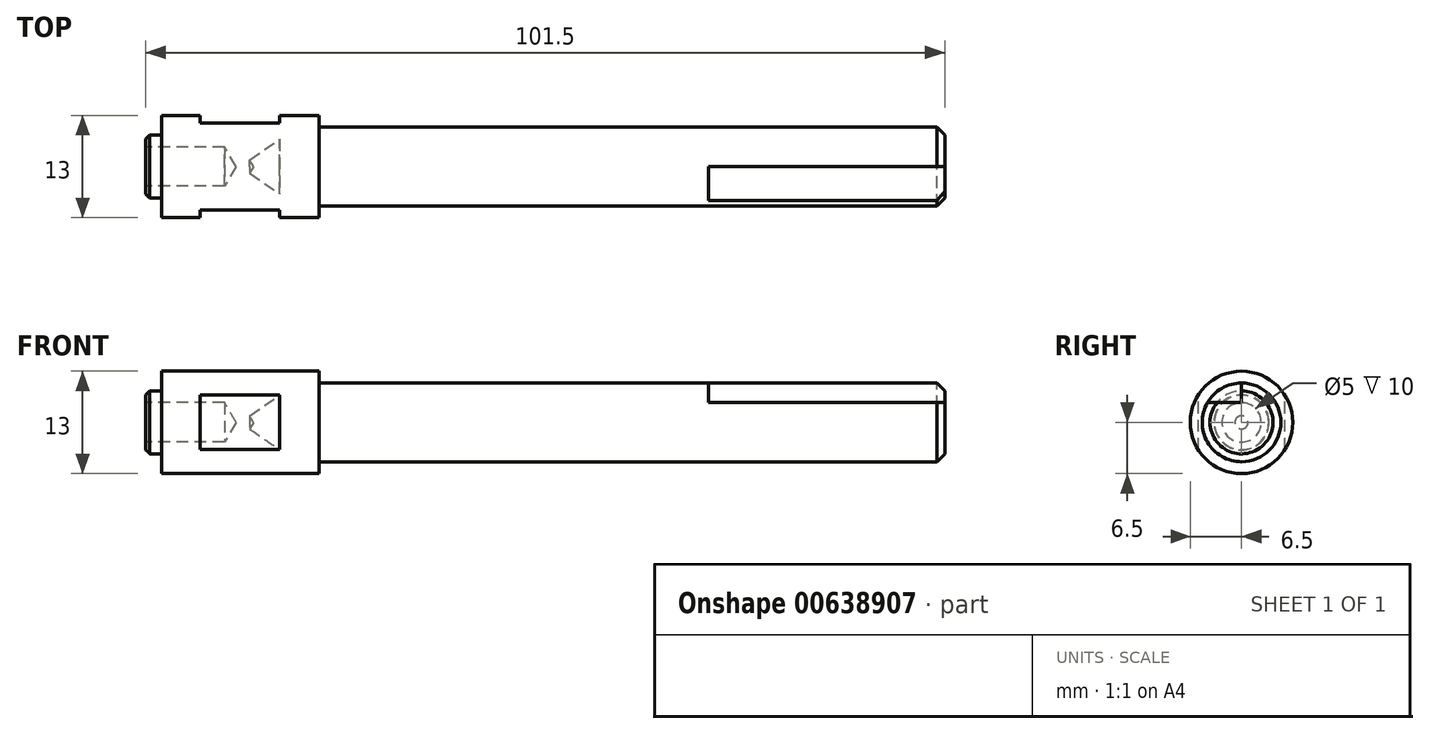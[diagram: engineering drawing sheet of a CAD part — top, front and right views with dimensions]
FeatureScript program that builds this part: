
annotation { "Feature Type Name" : "Feature", "Feature Type Description" : "" }
export const myFeature = defineFeature(function(context is Context, id is Id, definition is map)
    precondition{}
    {
        {
            var Q0;
            Q0=qCreatedBy(makeId("Front.planeOp"),FACE);
            var sketch = newSketch(context, id + "F0", { "sketchPlane" : qUnion([Q0])});
            skLineSegment(sketch, "E0", {"start": v(98.5, 5) * mm, "end": v(20, 5) * mm});
            skLineSegment(sketch, "E1", {"start": v(-2, 0) * mm, "end": v(99.5, 0) * mm});
            skLineSegment(sketch, "E2", {"start": v(98.5, -5) * mm, "end": v(20, -5) * mm});
            skLineSegment(sketch, "E3", {"start": v(99.5, -4) * mm, "end": v(98.5, -5) * mm});
            skLineSegment(sketch, "E4", {"start": v(99.5, 4) * mm, "end": v(98.5, 5) * mm});
            skLineSegment(sketch, "E5", {"start": v(99.5, -4) * mm, "end": v(99.5, 4) * mm});
            skLineSegment(sketch, "E6", {"start": v(98.5, 5) * mm, "end": v(98.5, -5) * mm});
            skLineSegment(sketch, "E7", {"start": v(20, -6.5) * mm, "end": v(20, 6.5) * mm});
            skLineSegment(sketch, "E8", {"start": v(-2, 2.07) * mm, "end": v(10.5, 2.07) * mm});
            skLineSegment(sketch, "E9", {"start": v(10.5, 2.07) * mm, "end": v(10.5, -2.06) * mm});
            skLineSegment(sketch, "E10", {"start": v(10.5, -2.06) * mm, "end": v(-2, -2.06) * mm});
            skLineSegment(sketch, "E11", {"start": v(10.5, -2.06) * mm, "end": v(11.7, 0) * mm});
            skLineSegment(sketch, "E12", {"start": v(10.5, 2.07) * mm, "end": v(11.7, 0) * mm});
            skLineSegment(sketch, "E13", {"start": v(8, 2.5) * mm, "end": v(8, -2.5) * mm});
            skLineSegment(sketch, "E14", {"start": v(8, -2.5) * mm, "end": v(-2, -2.5) * mm});
            skLineSegment(sketch, "E15", {"start": v(-2, 2.5) * mm, "end": v(8, 2.5) * mm});
            skLineSegment(sketch, "E16", {"start": v(8, -2.5) * mm, "end": v(8.75, -2.06) * mm});
            skLineSegment(sketch, "E17", {"start": v(8, 2.5) * mm, "end": v(8.75, 2.07) * mm});
            skLineSegment(sketch, "E18", {"start": v(13.06, 0) * mm, "end": v(-3.37, 0) * mm});
            skLineSegment(sketch, "E19", {"start": v(-1.5, -4) * mm, "end": v(0, -4) * mm});
            skLineSegment(sketch, "E20", {"start": v(-1.5, 4) * mm, "end": v(0, 4) * mm});
            skLineSegment(sketch, "E21", {"start": v(0, -6.5) * mm, "end": v(0, 6.5) * mm});
            skLineSegment(sketch, "E22", {"start": v(15, -3.46) * mm, "end": v(5, -3.46) * mm});
            skLineSegment(sketch, "E23", {"start": v(5, -3.46) * mm, "end": v(5, 3.46) * mm});
            skLineSegment(sketch, "E24", {"start": v(15, -3.46) * mm, "end": v(15, 3.46) * mm});
            skLineSegment(sketch, "E25", {"start": v(15, 3.46) * mm, "end": v(5, 3.46) * mm});
            skLineSegment(sketch, "E26", {"start": v(5, -3.46) * mm, "end": v(15, 3.46) * mm});
            skLineSegment(sketch, "E27", {"start": v(5, 3.46) * mm, "end": v(15, -3.46) * mm});
            skLineSegment(sketch, "E28", {"start": v(0, 6.5) * mm, "end": v(20, 6.5) * mm});
            skLineSegment(sketch, "E29", {"start": v(0, -6.5) * mm, "end": v(20, -6.5) * mm});
            skLineSegment(sketch, "E30", {"start": v(-1.5, 4) * mm, "end": v(-2, 3.5) * mm});
            skLineSegment(sketch, "E31", {"start": v(-2, -3.5) * mm, "end": v(-1.5, -4) * mm});
            skLineSegment(sketch, "E32", {"start": v(-2, -3.5) * mm, "end": v(-2, 3.5) * mm});
            skLineSegment(sketch, "E33", {"start": v(-1.5, -4) * mm, "end": v(-1.5, 4) * mm});
            skCircle(sketch, "E34", {"center": v(136.71, 38.37) * mm, "radius": 5 * mm});
            skLineSegment(sketch, "E35", {"start": v(139.21, 42.7) * mm, "end": v(139.21, 34.04) * mm});
            skArc(sketch, "E36", {"start": v(139.21, 41.49) * mm, "mid": v(132.71, 38.37) * mm, "end": v(139.21, 35.24) * mm});
            skLineSegment(sketch, "E37", {"start": v(133.25, 43.87) * mm, "end": v(140.18, 43.87) * mm});
            skLineSegment(sketch, "E38", {"start": v(133.25, 32.87) * mm, "end": v(140.18, 32.87) * mm});
            skCircle(sketch, "E39", {"center": v(136.71, 38.37) * mm, "radius": 6.5 * mm});
            skLineSegment(sketch, "E40", {"start": v(136.71, 45.37) * mm, "end": v(136.71, 31.37) * mm});
            skLineSegment(sketch, "E41", {"start": v(129.71, 38.37) * mm, "end": v(143.71, 38.37) * mm});
            skLineSegment(sketch, "E42", {"start": v(98.5, 43.37) * mm, "end": v(20, 43.37) * mm});
            skLineSegment(sketch, "E43", {"start": v(-2, 38.37) * mm, "end": v(99.5, 38.37) * mm});
            skLineSegment(sketch, "E44", {"start": v(98.5, 33.37) * mm, "end": v(20, 33.37) * mm});
            skLineSegment(sketch, "E45", {"start": v(99.5, 34.37) * mm, "end": v(98.5, 33.37) * mm});
            skLineSegment(sketch, "E46", {"start": v(99.5, 42.37) * mm, "end": v(98.5, 43.37) * mm});
            skLineSegment(sketch, "E47", {"start": v(99.5, 34.37) * mm, "end": v(99.5, 42.37) * mm});
            skLineSegment(sketch, "E48", {"start": v(98.5, 43.37) * mm, "end": v(98.5, 33.37) * mm});
            skLineSegment(sketch, "E49", {"start": v(20, 31.87) * mm, "end": v(20, 44.87) * mm});
            skLineSegment(sketch, "E50", {"start": v(-2, 40.43) * mm, "end": v(10.5, 40.43) * mm});
            skLineSegment(sketch, "E51", {"start": v(10.5, 40.43) * mm, "end": v(10.5, 36.3) * mm});
            skLineSegment(sketch, "E52", {"start": v(10.5, 36.3) * mm, "end": v(-2, 36.3) * mm});
            skLineSegment(sketch, "E53", {"start": v(10.5, 36.3) * mm, "end": v(11.7, 38.37) * mm});
            skLineSegment(sketch, "E54", {"start": v(10.5, 40.43) * mm, "end": v(11.7, 38.37) * mm});
            skLineSegment(sketch, "E55", {"start": v(8, 40.87) * mm, "end": v(8, 35.87) * mm});
            skLineSegment(sketch, "E56", {"start": v(8, 35.87) * mm, "end": v(-2, 35.87) * mm});
            skLineSegment(sketch, "E57", {"start": v(-2, 40.87) * mm, "end": v(8, 40.87) * mm});
            skLineSegment(sketch, "E58", {"start": v(8, 35.87) * mm, "end": v(8.75, 36.3) * mm});
            skLineSegment(sketch, "E59", {"start": v(8, 40.87) * mm, "end": v(8.75, 40.43) * mm});
            skLineSegment(sketch, "E60", {"start": v(13.06, 38.37) * mm, "end": v(-3.37, 38.37) * mm});
            skLineSegment(sketch, "E61", {"start": v(-1.5, 34.37) * mm, "end": v(0, 34.37) * mm});
            skLineSegment(sketch, "E62", {"start": v(-1.5, 42.37) * mm, "end": v(0, 42.37) * mm});
            skLineSegment(sketch, "E63", {"start": v(0, 31.87) * mm, "end": v(0, 44.87) * mm});
            skLineSegment(sketch, "E64", {"start": v(0, 44.87) * mm, "end": v(4.94, 44.87) * mm});
            skLineSegment(sketch, "E65", {"start": v(0, 31.87) * mm, "end": v(4.94, 31.87) * mm});
            skLineSegment(sketch, "E66", {"start": v(-1.5, 42.37) * mm, "end": v(-2, 41.87) * mm});
            skLineSegment(sketch, "E67", {"start": v(-2, 34.87) * mm, "end": v(-1.5, 34.37) * mm});
            skLineSegment(sketch, "E68", {"start": v(-2, 34.87) * mm, "end": v(-2, 41.87) * mm});
            skLineSegment(sketch, "E69", {"start": v(-1.5, 34.37) * mm, "end": v(-1.5, 42.37) * mm});
            skLineSegment(sketch, "E70", {"start": v(15, 31.87) * mm, "end": v(15, 32.87) * mm});
            skLineSegment(sketch, "E71", {"start": v(4.94, 31.87) * mm, "end": v(4.94, 32.87) * mm});
            skLineSegment(sketch, "E72", {"start": v(15, 43.87) * mm, "end": v(4.94, 43.87) * mm});
            skLineSegment(sketch, "E73", {"start": v(15, 32.87) * mm, "end": v(4.94, 32.87) * mm});
            skLineSegment(sketch, "E74", {"start": v(15, 43.87) * mm, "end": v(15, 44.87) * mm});
            skLineSegment(sketch, "E75", {"start": v(4.94, 43.87) * mm, "end": v(4.94, 44.87) * mm});
            skLineSegment(sketch, "E76", {"start": v(15, 44.87) * mm, "end": v(20, 44.87) * mm});
            skLineSegment(sketch, "E77", {"start": v(15, 31.87) * mm, "end": v(20, 31.87) * mm});
            skLineSegment(sketch, "E78", {"start": v(69.5, 33.37) * mm, "end": v(69.5, 43.37) * mm});
            skSolve(sketch);
        }
        {
            var Q0;
            {var subQ11=sQuery(id+"F0.wireOp",EDGE,"E25");Q0=makeQuery(id+"F0.imprint","IMPRINT",FACE,{"disambiguationData":[TD([[makeQuery(id+"F0.imprint","IMPRINT",EDGE,{"derivedFrom":subQ11}),-1.0]])]});}
            var Q1;
            {var subQ5=sQuery(id+"F0.wireOp",EDGE,"E20");Q1=makeQuery(id+"F0.imprint","IMPRINT",FACE,{"disambiguationData":[TD([[makeQuery(id+"F0.imprint","IMPRINT",EDGE,{"derivedFrom":subQ5}),-1.0]])]});}
            var Q2;
            {var subQ0=sQuery(id+"F0.wireOp",EDGE,"E17");Q2=makeQuery(id+"F0.imprint","IMPRINT",FACE,{"disambiguationData":[TD([[makeQuery(id+"F0.imprint","IMPRINT",EDGE,{"derivedFrom":subQ0}),1.0]])]});}
            var Q3;
            {var subQ3=sQuery(id+"F0.wireOp",EDGE,"E1");var subQ5=sQuery(id+"F0.wireOp",EDGE,"E18");var subQ9=makeQuery(id+"F0.imprint","INTERSECT",VERTEX,{"derivedFrom":[subQ3,subQ5]});Q3=makeQuery(id+"F0.imprint","IMPRINT",FACE,{"disambiguationData":[TD([[makeQuery(id+"F0.imprint","IMPRINT",EDGE,{"disambiguationData":[TD([[subQ9,-1.0]])],"derivedFrom":subQ3}),1.0]])]});}
            var Q4;
            {var subQ1=sQuery(id+"F0.wireOp",EDGE,"E9");var subQ3=sQuery(id+"F0.wireOp",EDGE,"E26");var subQ4=makeQuery(id+"F0.imprint","INTERSECT",VERTEX,{"derivedFrom":[subQ1,subQ3]});Q4=makeQuery(id+"F0.imprint","IMPRINT",FACE,{"disambiguationData":[TD([[makeQuery(id+"F0.imprint","IMPRINT",EDGE,{"disambiguationData":[TD([[subQ4,-1.0]])],"derivedFrom":subQ3}),1.0]])]});}
            var Q5;
            {var subQ0=sQuery(id+"F0.wireOp",EDGE,"E23");var subQ1=sQuery(id+"F0.wireOp",EDGE,"E8");var subQ2=makeQuery(id+"F0.imprint","INTERSECT",VERTEX,{"derivedFrom":[subQ1,subQ0]});Q5=makeQuery(id+"F0.imprint","IMPRINT",FACE,{"disambiguationData":[TD([[makeQuery(id+"F0.imprint","IMPRINT",EDGE,{"disambiguationData":[TD([[subQ2,-1.0]])],"derivedFrom":subQ1}),-1.0]])]});}
            var Q6;
            {var subQ0=sQuery(id+"F0.wireOp",EDGE,"E33");var subQ1=sQuery(id+"F0.wireOp",EDGE,"E8");var subQ2=makeQuery(id+"F0.imprint","INTERSECT",VERTEX,{"derivedFrom":[subQ1,subQ0]});Q6=makeQuery(id+"F0.imprint","IMPRINT",FACE,{"disambiguationData":[TD([[makeQuery(id+"F0.imprint","IMPRINT",EDGE,{"disambiguationData":[TD([[subQ2,-1.0]])],"derivedFrom":subQ1}),-1.0]])]});}
            var Q7;
            {var subQ0=sQuery(id+"F0.wireOp",EDGE,"E21");var subQ1=sQuery(id+"F0.wireOp",EDGE,"E8");var subQ2=makeQuery(id+"F0.imprint","INTERSECT",VERTEX,{"derivedFrom":[subQ1,subQ0]});Q7=makeQuery(id+"F0.imprint","IMPRINT",FACE,{"disambiguationData":[TD([[makeQuery(id+"F0.imprint","IMPRINT",EDGE,{"disambiguationData":[TD([[subQ2,-1.0]])],"derivedFrom":subQ1}),-1.0]])]});}
            var Q8;
            {var subQ5=sQuery(id+"F0.wireOp",EDGE,"E4");Q8=makeQuery(id+"F0.imprint","IMPRINT",FACE,{"disambiguationData":[TD([[makeQuery(id+"F0.imprint","IMPRINT",EDGE,{"derivedFrom":subQ5}),1.0]])]});}
            var Q9;
            {var subQ0=sQuery(id+"F0.wireOp",EDGE,"E0");Q9=makeQuery(id+"F0.imprint","IMPRINT",FACE,{"disambiguationData":[TD([[makeQuery(id+"F0.imprint","IMPRINT",EDGE,{"derivedFrom":subQ0}),1.0]])]});}
            var Q10;
            {var subQ1=sQuery(id+"F0.wireOp",EDGE,"E8");var subQ10=makeQuery(id+"F0.imprint","INTERSECT",VERTEX,{"derivedFrom":[subQ1,sQuery(id+"F0.wireOp",EDGE,"E17")]});Q10=makeQuery(id+"F0.imprint","IMPRINT",FACE,{"disambiguationData":[TD([[makeQuery(id+"F0.imprint","IMPRINT",EDGE,{"disambiguationData":[TD([[subQ10,1.0]])],"derivedFrom":subQ1}),-1.0]])]});}
            var Q11;
            {var subQ0=sQuery(id+"F0.wireOp",EDGE,"E23");var subQ1=sQuery(id+"F0.wireOp",EDGE,"E15");var subQ2=makeQuery(id+"F0.imprint","INTERSECT",VERTEX,{"derivedFrom":[subQ1,subQ0]});Q11=makeQuery(id+"F0.imprint","IMPRINT",FACE,{"disambiguationData":[TD([[makeQuery(id+"F0.imprint","IMPRINT",EDGE,{"disambiguationData":[TD([[subQ2,-1.0]])],"derivedFrom":subQ1}),1.0]])]});}
            var Q12;
            {var subQ0=sQuery(id+"F0.wireOp",EDGE,"E27");var subQ1=sQuery(id+"F0.wireOp",EDGE,"E13");var subQ2=makeQuery(id+"F0.imprint","INTERSECT",VERTEX,{"derivedFrom":[subQ1,subQ0]});Q12=makeQuery(id+"F0.imprint","IMPRINT",FACE,{"disambiguationData":[TD([[makeQuery(id+"F0.imprint","IMPRINT",EDGE,{"disambiguationData":[TD([[subQ2,-1.0]])],"derivedFrom":subQ1}),1.0]])]});}
            var Q13;
            {var subQ0=sQuery(id+"F0.wireOp",EDGE,"E27");var subQ1=sQuery(id+"F0.wireOp",EDGE,"E8");var subQ2=makeQuery(id+"F0.imprint","INTERSECT",VERTEX,{"derivedFrom":[subQ1,subQ0]});Q13=makeQuery(id+"F0.imprint","IMPRINT",FACE,{"disambiguationData":[TD([[makeQuery(id+"F0.imprint","IMPRINT",EDGE,{"disambiguationData":[TD([[subQ2,-1.0]])],"derivedFrom":subQ1}),-1.0]])]});}
            var Q14;
            {var subQ0=sQuery(id+"F0.wireOp",EDGE,"E33");var subQ1=sQuery(id+"F0.wireOp",EDGE,"E8");var subQ2=makeQuery(id+"F0.imprint","INTERSECT",VERTEX,{"derivedFrom":[subQ1,subQ0]});Q14=makeQuery(id+"F0.imprint","IMPRINT",FACE,{"disambiguationData":[TD([[makeQuery(id+"F0.imprint","IMPRINT",EDGE,{"disambiguationData":[TD([[subQ2,-1.0]])],"derivedFrom":subQ1}),1.0]])]});}
            var Q15;
            {var subQ0=sQuery(id+"F0.wireOp",EDGE,"E21");var subQ1=sQuery(id+"F0.wireOp",EDGE,"E8");var subQ2=makeQuery(id+"F0.imprint","INTERSECT",VERTEX,{"derivedFrom":[subQ1,subQ0]});Q15=makeQuery(id+"F0.imprint","IMPRINT",FACE,{"disambiguationData":[TD([[makeQuery(id+"F0.imprint","IMPRINT",EDGE,{"disambiguationData":[TD([[subQ2,-1.0]])],"derivedFrom":subQ1}),1.0]])]});}
            var Q16;
            {var subQ0=sQuery(id+"F0.wireOp",EDGE,"E23");var subQ1=sQuery(id+"F0.wireOp",EDGE,"E8");var subQ2=makeQuery(id+"F0.imprint","INTERSECT",VERTEX,{"derivedFrom":[subQ1,subQ0]});Q16=makeQuery(id+"F0.imprint","IMPRINT",FACE,{"disambiguationData":[TD([[makeQuery(id+"F0.imprint","IMPRINT",EDGE,{"disambiguationData":[TD([[subQ2,-1.0]])],"derivedFrom":subQ1}),1.0]])]});}
            var Q17;
            {var subQ0=sQuery(id+"F0.wireOp",EDGE,"E32");var subQ1=sQuery(id+"F0.wireOp",EDGE,"E8");var subQ2=makeQuery(id+"F0.imprint","INTERSECT",VERTEX,{"derivedFrom":[subQ1,subQ0]});Q17=makeQuery(id+"F0.imprint","IMPRINT",FACE,{"disambiguationData":[TD([[makeQuery(id+"F0.imprint","IMPRINT",EDGE,{"disambiguationData":[TD([[subQ2,-1.0]])],"derivedFrom":subQ1}),-1.0]])]});}
            var Q18;
            {var subQ0=sQuery(id+"F0.wireOp",EDGE,"E27");var subQ1=sQuery(id+"F0.wireOp",EDGE,"E8");var subQ2=makeQuery(id+"F0.imprint","INTERSECT",VERTEX,{"derivedFrom":[subQ1,subQ0]});Q18=makeQuery(id+"F0.imprint","IMPRINT",FACE,{"disambiguationData":[TD([[makeQuery(id+"F0.imprint","IMPRINT",EDGE,{"disambiguationData":[TD([[subQ2,-1.0]])],"derivedFrom":subQ1}),1.0]])]});}
            var Q19;
            {var subQ0=sQuery(id+"F0.wireOp",EDGE,"E17");Q19=makeQuery(id+"F0.imprint","IMPRINT",FACE,{"disambiguationData":[TD([[makeQuery(id+"F0.imprint","IMPRINT",EDGE,{"derivedFrom":subQ0}),-1.0]])]});}
            var Q20;
            {var subQ0=sQuery(id+"F0.wireOp",EDGE,"E32");var subQ1=sQuery(id+"F0.wireOp",EDGE,"E8");var subQ2=makeQuery(id+"F0.imprint","INTERSECT",VERTEX,{"derivedFrom":[subQ1,subQ0]});Q20=makeQuery(id+"F0.imprint","IMPRINT",FACE,{"disambiguationData":[TD([[makeQuery(id+"F0.imprint","IMPRINT",EDGE,{"disambiguationData":[TD([[subQ2,-1.0]])],"derivedFrom":subQ1}),1.0]])]});}
            var Q21;
            {var subQ5=sQuery(id+"F0.wireOp",EDGE,"E30");Q21=makeQuery(id+"F0.imprint","IMPRINT",FACE,{"disambiguationData":[TD([[makeQuery(id+"F0.imprint","IMPRINT",EDGE,{"derivedFrom":subQ5}),1.0]])]});}
            var Q22;
            {var subQ0=sQuery(id+"F0.wireOp",EDGE,"E26");var subQ1=sQuery(id+"F0.wireOp",EDGE,"E9");var subQ2=makeQuery(id+"F0.imprint","INTERSECT",VERTEX,{"derivedFrom":[subQ1,subQ0]});Q22=makeQuery(id+"F0.imprint","IMPRINT",FACE,{"disambiguationData":[TD([[makeQuery(id+"F0.imprint","IMPRINT",EDGE,{"disambiguationData":[TD([[subQ2,-1.0]])],"derivedFrom":subQ1}),1.0]])]});}
            var Q23;
            {var subQ0=sQuery(id+"F0.wireOp",EDGE,"E26");var subQ1=sQuery(id+"F0.wireOp",EDGE,"E9");var subQ2=makeQuery(id+"F0.imprint","INTERSECT",VERTEX,{"derivedFrom":[subQ1,subQ0]});Q23=makeQuery(id+"F0.imprint","IMPRINT",FACE,{"disambiguationData":[TD([[makeQuery(id+"F0.imprint","IMPRINT",EDGE,{"disambiguationData":[TD([[subQ2,-1.0]])],"derivedFrom":subQ1}),-1.0]])]});}
            var Q24;
            Q24=sQuery(id+"F0.wireOp",EDGE,"E18");
            revolve(context, id + "F1", {"entities" : qUnion([Q0, Q1, Q2, Q3, Q4, Q5, Q6, Q7, Q8, Q9, Q10, Q11, Q12, Q13, Q14, Q15, Q16, Q17, Q18, Q19, Q20, Q21, Q22, Q23]), "axis" : qUnion([Q24]), "revolveType" : RevolveType.FULL});
        }
        {
            var Q0;
            Q0=makeQuery(id+"F1.opRevolve","SWEPT_FACE",FACE,{"disambiguationData":[OSD([sQuery(id+"F0.wireOp",EDGE,"E32")])]});
            var sketch = newSketch(context, id + "F2", { "sketchPlane" : qUnion([Q0])});
            skCircle(sketch, "E79.0.0", {"center": v(0, 0) * mm, "radius": 3.5 * mm});
            skSolve(sketch);
        }
        {
            var Q0;
            Q0=sQuery(id+"F2.wireOp",VERTEX,"E79.0.0.center");
            var Q1;
            Q1=makeQuery(id+"F1.opRevolve","SWEPT_BODY",BODY,{"disambiguationData":[OSD([sQuery(id+"F0.wireOp",EDGE,"E0"),sQuery(id+"F0.wireOp",EDGE,"E1"),sQuery(id+"F0.wireOp",EDGE,"E4"),sQuery(id+"F0.wireOp",EDGE,"E5"),sQuery(id+"F0.wireOp",EDGE,"E7"),sQuery(id+"F0.wireOp",EDGE,"E18"),sQuery(id+"F0.wireOp",EDGE,"E20"),sQuery(id+"F0.wireOp",EDGE,"E21"),sQuery(id+"F0.wireOp",EDGE,"E28"),sQuery(id+"F0.wireOp",EDGE,"E30"),sQuery(id+"F0.wireOp",EDGE,"E32")])]});
            hole(context, id + "F3", {"style" : HoleStyle.SIMPLE, "endStyle" : HoleEndStyle.BLIND, "holeDiameter" : 5 * mm, "majorDiameter" : 5 * mm, "holeDepth" : 10 * mm, "isTappedThrough" : true, "tappedDepth" : 12 * mm, "tapClearance" : 3, "locations" : qUnion([Q0]), "scope" : qUnion([Q1])});
        }
        {
            var Q0;
            Q0=qCreatedBy(makeId("Top.planeOp"),FACE);
            var sketch = newSketch(context, id + "F4", { "sketchPlane" : qUnion([Q0])});
            skLineSegment(sketch, "E80", {"start": v(98.5, 5) * mm, "end": v(20, 5) * mm});
            skLineSegment(sketch, "E81", {"start": v(-2, 0) * mm, "end": v(99.5, 0) * mm});
            skLineSegment(sketch, "E82", {"start": v(98.5, -5) * mm, "end": v(20, -5) * mm});
            skLineSegment(sketch, "E83", {"start": v(99.5, -4) * mm, "end": v(98.5, -5) * mm});
            skLineSegment(sketch, "E84", {"start": v(99.5, 4) * mm, "end": v(98.5, 5) * mm});
            skLineSegment(sketch, "E85", {"start": v(99.5, -4) * mm, "end": v(99.5, 4) * mm});
            skLineSegment(sketch, "E86", {"start": v(98.5, 5) * mm, "end": v(98.5, -5) * mm});
            skLineSegment(sketch, "E87", {"start": v(20, -6.5) * mm, "end": v(20, 6.5) * mm});
            skLineSegment(sketch, "E88", {"start": v(-2, 2.06) * mm, "end": v(10.5, 2.06) * mm});
            skLineSegment(sketch, "E89", {"start": v(10.5, 2.06) * mm, "end": v(10.5, -2.06) * mm});
            skLineSegment(sketch, "E90", {"start": v(10.5, -2.06) * mm, "end": v(-2, -2.06) * mm});
            skLineSegment(sketch, "E91", {"start": v(10.5, -2.06) * mm, "end": v(11.7, 0) * mm});
            skLineSegment(sketch, "E92", {"start": v(10.5, 2.06) * mm, "end": v(11.7, 0) * mm});
            skLineSegment(sketch, "E93", {"start": v(8, 2.5) * mm, "end": v(8, -2.5) * mm});
            skLineSegment(sketch, "E94", {"start": v(8, -2.5) * mm, "end": v(-2, -2.5) * mm});
            skLineSegment(sketch, "E95", {"start": v(-2, 2.5) * mm, "end": v(8, 2.5) * mm});
            skLineSegment(sketch, "E96", {"start": v(8, -2.5) * mm, "end": v(8.75, -2.06) * mm});
            skLineSegment(sketch, "E97", {"start": v(8, 2.5) * mm, "end": v(8.75, 2.07) * mm});
            skLineSegment(sketch, "E98", {"start": v(13.06, 0) * mm, "end": v(-3.37, 0) * mm});
            skLineSegment(sketch, "E99", {"start": v(-1.5, -4) * mm, "end": v(0, -4) * mm});
            skLineSegment(sketch, "E100", {"start": v(-1.5, 4) * mm, "end": v(0, 4) * mm});
            skLineSegment(sketch, "E101", {"start": v(0, -6.5) * mm, "end": v(0, 6.5) * mm});
            skLineSegment(sketch, "E102", {"start": v(0, 6.5) * mm, "end": v(4.94, 6.5) * mm});
            skLineSegment(sketch, "E103", {"start": v(0, -6.5) * mm, "end": v(4.94, -6.5) * mm});
            skLineSegment(sketch, "E104", {"start": v(-1.5, 4) * mm, "end": v(-2, 3.5) * mm});
            skLineSegment(sketch, "E105", {"start": v(-2, -3.5) * mm, "end": v(-1.5, -4) * mm});
            skLineSegment(sketch, "E106", {"start": v(-2, -3.5) * mm, "end": v(-2, 3.5) * mm});
            skLineSegment(sketch, "E107", {"start": v(-1.5, -4) * mm, "end": v(-1.5, 4) * mm});
            skLineSegment(sketch, "E108", {"start": v(15, -6.5) * mm, "end": v(15, -5.5) * mm});
            skLineSegment(sketch, "E109", {"start": v(4.94, -6.5) * mm, "end": v(4.94, -5.5) * mm});
            skLineSegment(sketch, "E110", {"start": v(15, 5.5) * mm, "end": v(4.94, 5.5) * mm});
            skLineSegment(sketch, "E111", {"start": v(15, -5.5) * mm, "end": v(4.94, -5.5) * mm});
            skLineSegment(sketch, "E112", {"start": v(15, 5.5) * mm, "end": v(15, 6.5) * mm});
            skLineSegment(sketch, "E113", {"start": v(4.94, 5.5) * mm, "end": v(4.94, 6.5) * mm});
            skLineSegment(sketch, "E114", {"start": v(15, 6.5) * mm, "end": v(20, 6.5) * mm});
            skLineSegment(sketch, "E115", {"start": v(15, -6.5) * mm, "end": v(20, -6.5) * mm});
            skLineSegment(sketch, "E116", {"start": v(69.5, -5) * mm, "end": v(69.5, 5) * mm});
            skLineSegment(sketch, "E117", {"start": v(0, 6.5) * mm, "end": v(20, 6.5) * mm});
            skLineSegment(sketch, "E118", {"start": v(20, -6.5) * mm, "end": v(0, -6.5) * mm});
            skSolve(sketch);
        }
        {
            var Q0;
            {var subQ0=sQuery(id+"F4.wireOp",EDGE,"E108");Q0=makeQuery(id+"F4.imprint","IMPRINT",FACE,{"disambiguationData":[TD([[makeQuery(id+"F4.imprint","IMPRINT",EDGE,{"derivedFrom":subQ0}),1.0]])]});}
            var Q1;
            Q1=makeQuery(id+"F4.imprint","IMPRINT",FACE,{"disambiguationData":[TD([[makeQuery(id+"F4.imprint","IMPRINT",EDGE,{"derivedFrom":sQuery(id+"F4.wireOp",EDGE,"E110")}),-1.0]])]});
            extrude(context, id + "F5", {"entities" : qUnion([Q0, Q1]), "operationType" : NewBodyOperationType.REMOVE, "endBound" : BoundingType.SYMMETRIC, "oppositeDirection" : true, "depth" : 25 * mm, "offsetDistance" : 25 * mm});
        }
        {
            var Q0;
            Q0=makeQuery(id+"F1.opRevolve","SWEPT_FACE",FACE,{"disambiguationData":[OSD([sQuery(id+"F0.wireOp",EDGE,"E5")])]});
            var sketch = newSketch(context, id + "F6", { "sketchPlane" : qUnion([Q0])});
            skCircle(sketch, "E119.0", {"center": v(0, 0) * mm, "radius": 4 * mm});
            skCircle(sketch, "E120", {"center": v(0, 0) * mm, "radius": 5 * mm});
            skLineSegment(sketch, "E121", {"start": v(-4.33, 2.5) * mm, "end": v(4.33, 2.5) * mm});
            skArc(sketch, "E122", {"start": v(-3.12, 2.5) * mm, "mid": v(0, -4) * mm, "end": v(3.12, 2.5) * mm});
            skLineSegment(sketch, "E123", {"start": v(-5.5, -3.46) * mm, "end": v(-5.5, 3.46) * mm});
            skLineSegment(sketch, "E124", {"start": v(5.5, -3.46) * mm, "end": v(5.5, 3.46) * mm});
            skCircle(sketch, "E125", {"center": v(0, 0) * mm, "radius": 6.5 * mm});
            skLineSegment(sketch, "E126", {"start": v(-7, 0) * mm, "end": v(7, 0) * mm});
            skLineSegment(sketch, "E127", {"start": v(0, -7) * mm, "end": v(0, 7) * mm});
            skSolve(sketch);
        }
        {
            var Q0;
            {var subQ0=sQuery(id+"F6.wireOp",EDGE,"E121");var subQ1=sQuery(id+"F6.wireOp",EDGE,"E119.0");var subQ2=makeQuery(id+"F6.imprint","INTERSECT",VERTEX,{"disambiguationData":[OD(0.0)],"derivedFrom":[subQ1,subQ0]});Q0=makeQuery(id+"F6.imprint","IMPRINT",FACE,{"disambiguationData":[TD([[makeQuery(id+"F6.imprint","IMPRINT",EDGE,{"disambiguationData":[TD([[subQ2,-1.0]])],"derivedFrom":subQ1}),-1.0]])]});}
            var Q1;
            {var subQ0=sQuery(id+"F6.wireOp",EDGE,"E127");var subQ1=sQuery(id+"F6.wireOp",EDGE,"E119.0");var subQ2=makeQuery(id+"F6.imprint","INTERSECT",VERTEX,{"disambiguationData":[OD(1.0)],"derivedFrom":[subQ1,subQ0]});Q1=makeQuery(id+"F6.imprint","IMPRINT",FACE,{"disambiguationData":[TD([[makeQuery(id+"F6.imprint","IMPRINT",EDGE,{"disambiguationData":[TD([[subQ2,-1.0]])],"derivedFrom":subQ1}),-1.0]])]});}
            var Q2;
            {var subQ0=sQuery(id+"F6.wireOp",EDGE,"E127");var subQ1=sQuery(id+"F6.wireOp",EDGE,"E119.0");var subQ2=makeQuery(id+"F6.imprint","INTERSECT",VERTEX,{"disambiguationData":[OD(1.0)],"derivedFrom":[subQ1,subQ0]});Q2=makeQuery(id+"F6.imprint","IMPRINT",FACE,{"disambiguationData":[TD([[makeQuery(id+"F6.imprint","IMPRINT",EDGE,{"disambiguationData":[TD([[subQ2,-1.0]])],"derivedFrom":subQ1}),1.0]])]});}
            var Q3;
            {var subQ0=sQuery(id+"F6.wireOp",EDGE,"E121");var subQ1=sQuery(id+"F6.wireOp",EDGE,"E119.0");var subQ2=makeQuery(id+"F6.imprint","INTERSECT",VERTEX,{"disambiguationData":[OD(0.0)],"derivedFrom":[subQ1,subQ0]});Q3=makeQuery(id+"F6.imprint","IMPRINT",FACE,{"disambiguationData":[TD([[makeQuery(id+"F6.imprint","IMPRINT",EDGE,{"disambiguationData":[TD([[subQ2,-1.0]])],"derivedFrom":subQ1}),1.0]])]});}
            extrude(context, id + "F7", {"entities" : qUnion([Q0, Q1, Q2, Q3]), "operationType" : NewBodyOperationType.REMOVE, "oppositeDirection" : true, "depth" : 30 * mm, "offsetDistance" : 25 * mm});
        }
    });
